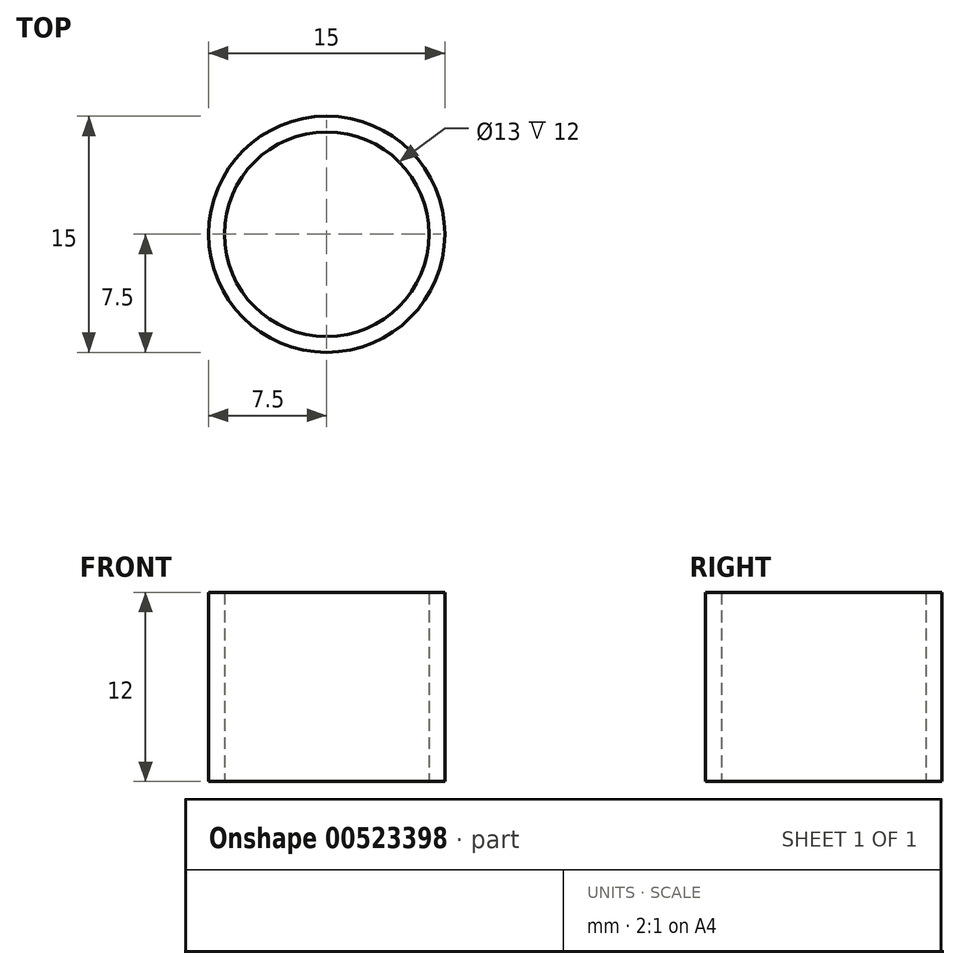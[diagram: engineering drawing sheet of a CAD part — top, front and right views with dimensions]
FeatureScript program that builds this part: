
annotation { "Feature Type Name" : "Feature", "Feature Type Description" : "" }
export const myFeature = defineFeature(function(context is Context, id is Id, definition is map)
    precondition{}
    {
        {
            var Q0;
            Q0=qCreatedBy(makeId("Top.planeOp"),FACE);
            var sketch = newSketch(context, id + "F0", { "sketchPlane" : qUnion([Q0])});
            skCircle(sketch, "E0", {"center": v(0, 0) * mm, "radius": 6.5 * mm});
            skCircle(sketch, "E1", {"center": v(0, 0) * mm, "radius": 7.5 * mm});
            skSolve(sketch);
        }
        {
            var Q0;
            Q0=qSketchRegion(id+"F0",true);
            extrude(context, id + "F1", {"entities" : qUnion([Q0]), "depth" : 12 * mm, "offsetDistance" : 25 * mm});
        }
    });
